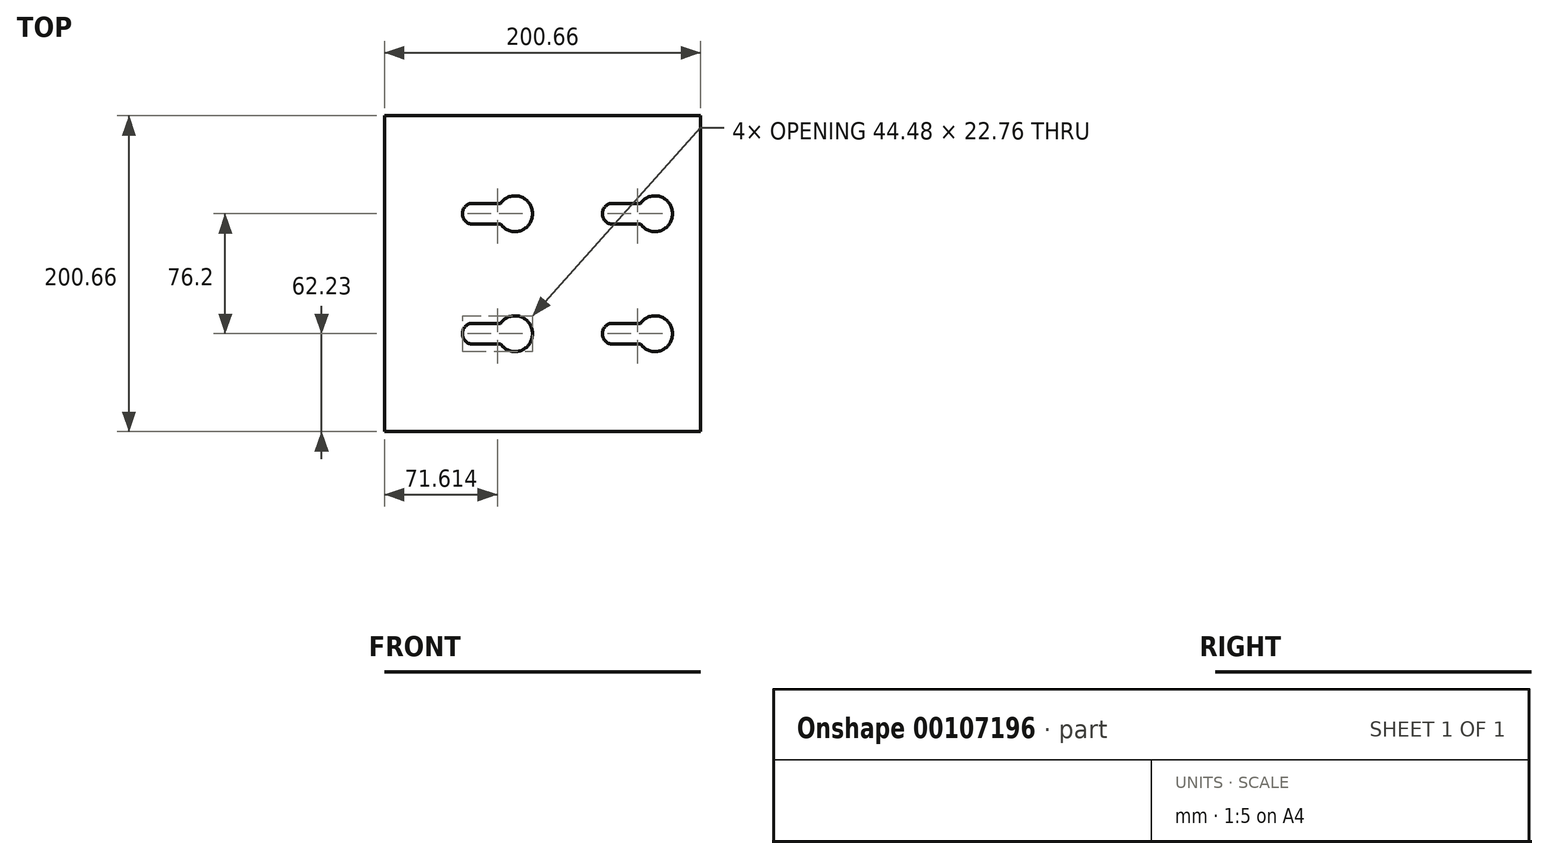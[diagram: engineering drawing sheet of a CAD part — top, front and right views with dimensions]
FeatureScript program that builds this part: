
annotation { "Feature Type Name" : "Feature", "Feature Type Description" : "" }
export const myFeature = defineFeature(function(context is Context, id is Id, definition is map)
    precondition{}
    {
        {
            var Q0;
            Q0=qCreatedBy(makeId("Top.planeOp"),FACE);
            var sketch = newSketch(context, id + "F0", { "sketchPlane" : qUnion([Q0])});
            skLineSegment(sketch, "E0.bottom", {"start": v(-100.33, 100.33) * mm, "end": v(100.33, 100.33) * mm});
            skLineSegment(sketch, "E0.top", {"start": v(-100.33, -100.33) * mm, "end": v(100.33, -100.33) * mm});
            skLineSegment(sketch, "E0.left", {"start": v(-100.33, 100.33) * mm, "end": v(-100.33, -100.33) * mm});
            skLineSegment(sketch, "E0.right", {"start": v(100.33, 100.33) * mm, "end": v(100.33, -100.33) * mm});
            skPoint(sketch, "E0.middle", {"position": v(0, 0) * mm});
            skPoint(sketch, "E1", {"position": v(-44.48, 38.23) * mm});
            skArc(sketch, "E2", {"start": v(-44.48, 44.7) * mm, "mid": v(-49.06, 42.8) * mm, "end": v(-50.96, 38.23) * mm});
            skLineSegment(sketch, "E3", {"start": v(-44.48, 44.7) * mm, "end": v(-30.04, 44.7) * mm});
            skLineSegment(sketch, "E4", {"start": v(-17.59, 38.37) * mm, "end": v(-17.59, 38.23) * mm});
            skLineSegment(sketch, "E5", {"start": v(-26.72, 44.7) * mm, "end": v(-30.04, 44.7) * mm});
            skArc(sketch, "E6", {"start": v(-6.48, 38.23) * mm, "mid": v(-14.2, 48.95) * mm, "end": v(-26.72, 44.7) * mm});
            skPoint(sketch, "E7.orphan", {"position": v(-17.59, 44.7) * mm});
            skLineSegment(sketch, "E8.MirrorCS", {"start": v(-17.59, 37.83) * mm, "end": v(-17.59, 37.97) * mm});
            skLineSegment(sketch, "E9.MirrorCS", {"start": v(-26.72, 31.5) * mm, "end": v(-30.04, 31.5) * mm});
            skArc(sketch, "E10.MirrorCS", {"start": v(-44.48, 31.5) * mm, "mid": v(-49.06, 33.4) * mm, "end": v(-50.96, 37.97) * mm});
            skLineSegment(sketch, "E11.MirrorCS", {"start": v(-44.48, 31.5) * mm, "end": v(-30.04, 31.5) * mm});
            skPoint(sketch, "E12.MirrorP", {"position": v(-17.59, 31.46) * mm});
            skArc(sketch, "E13.MirrorCS", {"start": v(-6.48, 37.97) * mm, "mid": v(-14.2, 27.25) * mm, "end": v(-26.72, 31.5) * mm});
            skPoint(sketch, "E14.0.1.0", {"position": v(-17.59, -31.5) * mm});
            skArc(sketch, "E14.0.1.1", {"start": v(-6.48, -38.23) * mm, "mid": v(-14.2, -48.95) * mm, "end": v(-26.72, -44.7) * mm});
            skPoint(sketch, "E14.0.1.2", {"position": v(-44.48, -38.23) * mm});
            skArc(sketch, "E14.0.1.3", {"start": v(-6.48, -37.97) * mm, "mid": v(-14.2, -27.25) * mm, "end": v(-26.72, -31.5) * mm});
            skLineSegment(sketch, "E14.0.1.4", {"start": v(-44.48, -44.7) * mm, "end": v(-30.04, -44.7) * mm});
            skPoint(sketch, "E14.0.1.5", {"position": v(-17.59, -44.74) * mm});
            skLineSegment(sketch, "E14.0.1.6", {"start": v(-44.48, -31.5) * mm, "end": v(-30.04, -31.5) * mm});
            skPoint(sketch, "E14.0.1.7", {"position": v(-44.48, -37.97) * mm});
            skArc(sketch, "E14.0.1.8", {"start": v(-44.48, -31.5) * mm, "mid": v(-49.06, -33.4) * mm, "end": v(-50.96, -37.97) * mm});
            skLineSegment(sketch, "E14.0.1.9", {"start": v(-26.72, -44.7) * mm, "end": v(-30.04, -44.7) * mm});
            skLineSegment(sketch, "E14.0.1.10", {"start": v(-26.72, -31.5) * mm, "end": v(-30.04, -31.5) * mm});
            skArc(sketch, "E14.0.1.11", {"start": v(-44.48, -44.7) * mm, "mid": v(-49.06, -42.8) * mm, "end": v(-50.96, -38.23) * mm});
            skLineSegment(sketch, "E14.0.1.12", {"start": v(-17.59, -38.37) * mm, "end": v(-17.59, -38.23) * mm});
            skLineSegment(sketch, "E14.0.1.13", {"start": v(-17.59, -37.83) * mm, "end": v(-17.59, -37.97) * mm});
            skPoint(sketch, "E14.1.0.0", {"position": v(71.31, 44.7) * mm});
            skArc(sketch, "E14.1.0.1", {"start": v(82.42, 37.97) * mm, "mid": v(74.7, 27.25) * mm, "end": v(62.18, 31.5) * mm});
            skPoint(sketch, "E14.1.0.2", {"position": v(44.42, 37.97) * mm});
            skArc(sketch, "E14.1.0.3", {"start": v(82.42, 38.23) * mm, "mid": v(74.7, 48.95) * mm, "end": v(62.18, 44.7) * mm});
            skPoint(sketch, "E14.1.0.5", {"position": v(71.31, 31.46) * mm});
            skLineSegment(sketch, "E14.1.0.6", {"start": v(44.42, 44.7) * mm, "end": v(58.86, 44.7) * mm});
            skPoint(sketch, "E14.1.0.7", {"position": v(44.42, 38.23) * mm});
            skArc(sketch, "E14.1.0.8", {"start": v(44.42, 44.7) * mm, "mid": v(39.84, 42.8) * mm, "end": v(37.94, 38.23) * mm});
            skLineSegment(sketch, "E14.1.0.9", {"start": v(62.18, 31.5) * mm, "end": v(58.86, 31.5) * mm});
            skLineSegment(sketch, "E14.1.0.10", {"start": v(62.18, 44.7) * mm, "end": v(58.86, 44.7) * mm});
            skArc(sketch, "E14.1.0.11", {"start": v(44.42, 31.5) * mm, "mid": v(39.84, 33.4) * mm, "end": v(37.94, 37.97) * mm});
            skLineSegment(sketch, "E14.1.0.12", {"start": v(71.31, 37.83) * mm, "end": v(71.31, 37.97) * mm});
            skLineSegment(sketch, "E14.1.0.13", {"start": v(71.31, 38.37) * mm, "end": v(71.31, 38.23) * mm});
            skPoint(sketch, "E14.1.1.0", {"position": v(71.31, -31.5) * mm});
            skArc(sketch, "E14.1.1.1", {"start": v(82.42, -38.23) * mm, "mid": v(74.7, -48.95) * mm, "end": v(62.18, -44.7) * mm});
            skPoint(sketch, "E14.1.1.2", {"position": v(44.42, -38.23) * mm});
            skArc(sketch, "E14.1.1.3", {"start": v(82.42, -37.97) * mm, "mid": v(74.7, -27.25) * mm, "end": v(62.18, -31.5) * mm});
            skLineSegment(sketch, "E14.1.1.4", {"start": v(44.42, -44.7) * mm, "end": v(58.86, -44.7) * mm});
            skPoint(sketch, "E14.1.1.5", {"position": v(71.31, -44.74) * mm});
            skLineSegment(sketch, "E14.1.1.6", {"start": v(44.42, -31.5) * mm, "end": v(58.86, -31.5) * mm});
            skPoint(sketch, "E14.1.1.7", {"position": v(44.42, -37.97) * mm});
            skArc(sketch, "E14.1.1.8", {"start": v(44.42, -31.5) * mm, "mid": v(39.84, -33.4) * mm, "end": v(37.94, -37.97) * mm});
            skLineSegment(sketch, "E14.1.1.9", {"start": v(62.18, -44.7) * mm, "end": v(58.86, -44.7) * mm});
            skLineSegment(sketch, "E14.1.1.10", {"start": v(62.18, -31.5) * mm, "end": v(58.86, -31.5) * mm});
            skArc(sketch, "E14.1.1.11", {"start": v(44.42, -44.7) * mm, "mid": v(39.84, -42.8) * mm, "end": v(37.94, -38.23) * mm});
            skLineSegment(sketch, "E14.1.1.12", {"start": v(71.31, -38.37) * mm, "end": v(71.31, -38.23) * mm});
            skLineSegment(sketch, "E14.1.1.13", {"start": v(71.31, -37.83) * mm, "end": v(71.31, -37.97) * mm});
            skLineSegment(sketch, "E14.direction1", {"start": v(-44.48, 31.5) * mm, "end": v(44.42, 31.5) * mm, "construction": true});
            skLineSegment(sketch, "E14.direction2", {"start": v(-44.48, 31.5) * mm, "end": v(-44.48, -44.7) * mm, "construction": true});
            skLineSegment(sketch, "E15", {"start": v(58.86, 31.5) * mm, "end": v(44.42, 31.5) * mm});
            skLineSegment(sketch, "E16", {"start": v(82.42, 38.23) * mm, "end": v(82.42, 37.97) * mm});
            skLineSegment(sketch, "E17", {"start": v(37.94, 38.23) * mm, "end": v(37.94, 37.97) * mm});
            skLineSegment(sketch, "E18", {"start": v(-6.48, 38.23) * mm, "end": v(-6.48, 37.97) * mm});
            skLineSegment(sketch, "E19", {"start": v(-50.96, 38.23) * mm, "end": v(-50.96, 37.97) * mm});
            skLineSegment(sketch, "E20", {"start": v(-6.48, -38.23) * mm, "end": v(-6.48, -37.97) * mm});
            skLineSegment(sketch, "E21", {"start": v(-50.96, -37.97) * mm, "end": v(-50.96, -38.23) * mm});
            skLineSegment(sketch, "E22", {"start": v(82.42, -37.97) * mm, "end": v(82.42, -38.23) * mm});
            skLineSegment(sketch, "E23", {"start": v(37.94, -37.97) * mm, "end": v(37.94, -38.23) * mm});
            skSolve(sketch);
        }
        {
            var Q0;
            Q0=makeQuery(id+"F0.imprint","IMPRINT",FACE,{"disambiguationData":[TD([[makeQuery(id+"F0.imprint","IMPRINT",EDGE,{"derivedFrom":sQuery(id+"F0.wireOp",EDGE,"E0.bottom")}),-1.0]])]});
            extrude(context, id + "F1", {"entities" : qUnion([Q0]), "depth" : 1 / 203.2 * mm});
        }
    });
